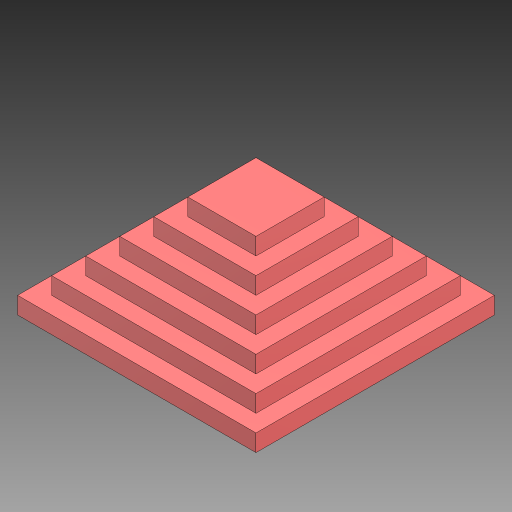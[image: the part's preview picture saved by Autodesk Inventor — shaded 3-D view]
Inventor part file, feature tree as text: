
AUTODESK INVENTOR PART (.ipt)
format: ipt  version: 2023 (Build 270158000, 158)  size: 425,472 bytes
history: native  units: mm
features: extrude x9, sketch x9, other x1
ambient origin geometry x8: Origin, YZ Plane, XZ Plane, XY Plane, X Axis, Y Axis, Z Axis, Center Point
bodies: Body1 (feature_tree)
feature tree (19):
  other  "Těleso1"
  extrude  "Vysunutí1"  Depth=210.0mm
  extrude  "Vysunutí2"  Depth=210.0mm
  extrude  "Vysunutí3"  Depth=15.0mm TaperAngle=0.0deg
  extrude  "Vysunutí4"  Depth=180.0mm
  extrude  "Vysunutí5"  Depth=180.0mm
  extrude  "Vysunutí6"  Depth=15.0mm TaperAngle=0.0deg
  extrude  "Vysunutí7"  Depth=150.0mm
  extrude  "Vysunutí8"  Depth=150.0mm
  extrude  "Vysunutí9"  Depth=15.0mm TaperAngle=0.0deg
  sketch  "Náčrt1"
  sketch  "Náčrt2"
  sketch  "Náčrt3"
  sketch  "Náčrt4"
  sketch  "Náčrt5"
  sketch  "Náčrt7"
  sketch  "Náčrt8"
  sketch  "Náčrt9"
  sketch  "Náčrt10"
